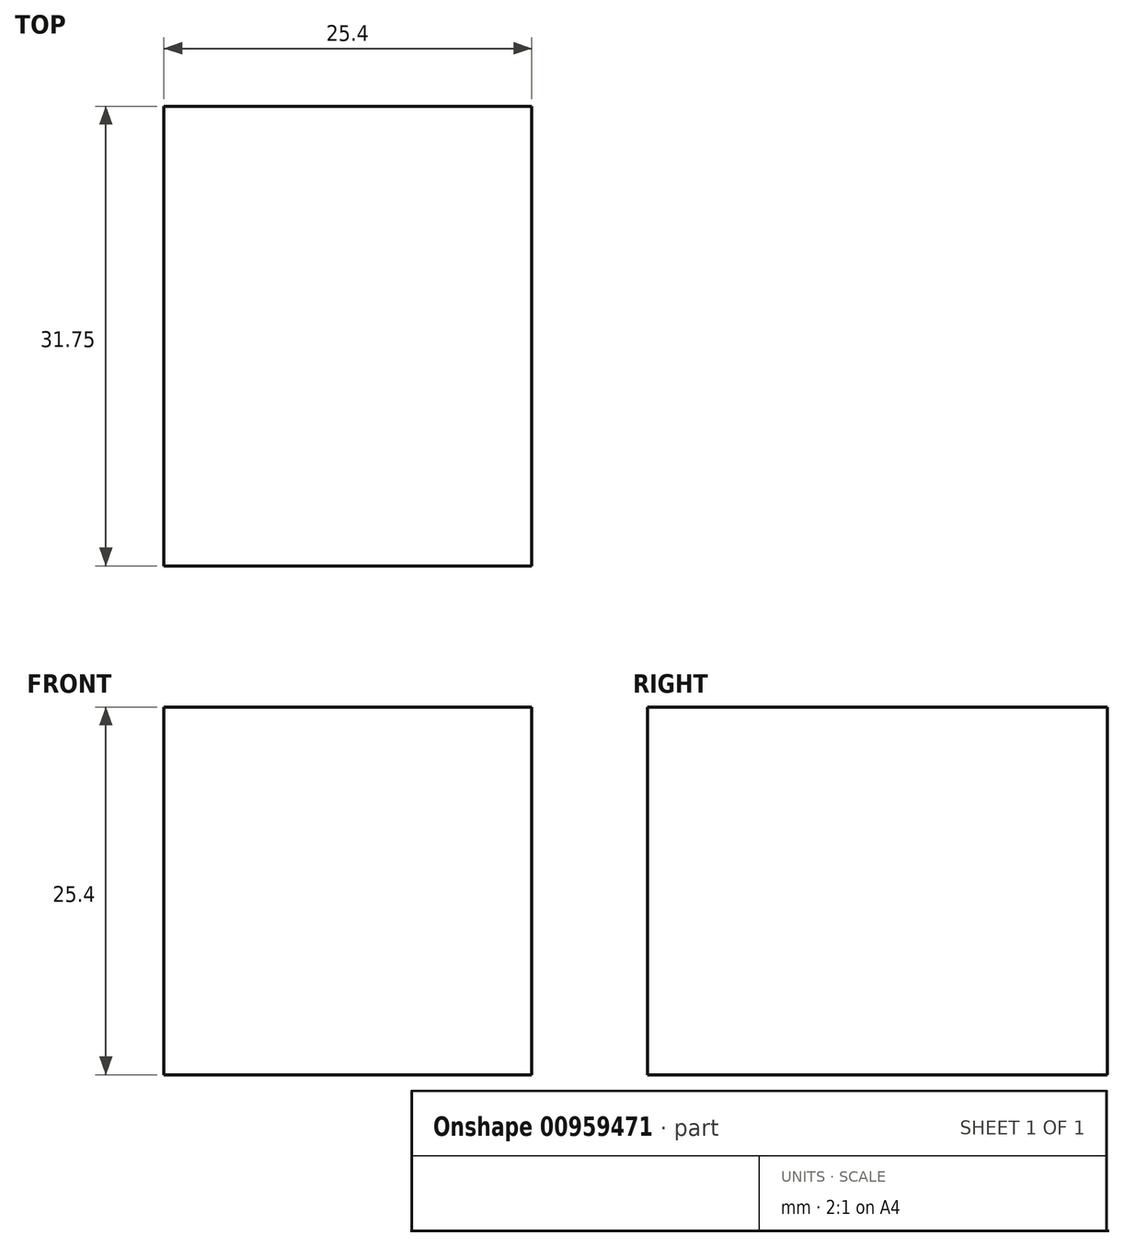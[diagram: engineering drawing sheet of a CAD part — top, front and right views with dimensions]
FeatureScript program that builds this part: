
annotation { "Feature Type Name" : "Feature", "Feature Type Description" : "" }
export const myFeature = defineFeature(function(context is Context, id is Id, definition is map)
    precondition{}
    {
        {
            var Q0;
            Q0=qCreatedBy(makeId("Top.planeOp"),FACE);
            var sketch = newSketch(context, id + "F0", { "sketchPlane" : qUnion([Q0])});
            skLineSegment(sketch, "E0.bottom", {"start": v(0, 0) * mm, "end": v(25.4, 0) * mm});
            skLineSegment(sketch, "E0.top", {"start": v(0, 31.75) * mm, "end": v(25.4, 31.75) * mm});
            skLineSegment(sketch, "E0.left", {"start": v(0, 0) * mm, "end": v(0, 31.75) * mm});
            skLineSegment(sketch, "E0.right", {"start": v(25.4, 0) * mm, "end": v(25.4, 31.75) * mm});
            skSolve(sketch);
        }
        {
            var Q0;
            Q0=makeQuery(id+"F0.imprint","IMPRINT",FACE,{"disambiguationData":[TD([[makeQuery(id+"F0.imprint","IMPRINT",EDGE,{"derivedFrom":sQuery(id+"F0.wireOp",EDGE,"E0.bottom")}),1.0]])]});
            extrude(context, id + "F1", {"entities" : qUnion([Q0]), "depth" : 25.4 * mm, "offsetDistance" : 25.4 * mm});
        }
    });
